# Revit family: MI-FISH
name_source: partatom
category: Plumbing Fixtures
units: mm (PartAtom-declared; Revit-internal decimal feet)

## family parameters
Classification Number = 23.45.30.00
Cut with Voids When Loaded = No
Enable Cutting in Views = No
Host = Face
Maintain Annotation Orientation = No
Part Type = Normal
Room Calculation Point = No
Round Connector Dimension = Use Radius
Shared = No

## types (12) — shared parameters
Assembly Code = D2090300
Description = Fish Scale Interceptor
Interceptor Material = Acid Resistant Epoxy Coated Green
Manufacturer = MIFAB
URL = www.mifab.com
zero-valued in all types: Default Elevation, WFU

## per-type parameters (varying)
| type | A | B | C | D | E | F | Standard Inlet And Outlet Radii | Water Capacity |
| MI-FISH-1 | 29.5 " | 20 " | 3 " | 17 " | 20 " | 2 " | 1 " | 34.29 Gallons |
| MI-FISH-2 | 29.5 " | 20.5 " | 4 " | 20 " | 24 " | 3 " | 1.5 " | 40.74 Gallons |
| MI-FISH-3 | 33.5 " | 26 " | 4 " | 26 " | 30 " | 3 " | 1.5 " | 80.18 Gallons |
| MI-FISH-4 | 37.5 " | 30 " | 4 " | 28 " | 32 " | 3 " | 1.5 " | 114.03 Gallons |
| MI-FISH-5 | 55.5 " | 26 " | 6 " | 30 " | 36 " | 4 " | 2 " | 155.64 Gallons |
| MI-FISH-6 | 67.5 " | 28 " | 8 " | 32 " | 40 " | 6 " | 3 " | 213.80 Gallons |
| MI-FISH-7 | 67.5 " | 28 " | 10 " | 44 " | 54 " | 6 " | 3 " | 302.26 Gallons |
| MI-FISH-8 | 67.5 " | 30 " | 12 " | 54 " | 66 " | 6 " | 3 " | 404.91 Gallons |
| MI-FISH-9 | 67.5 " | 40 " | 10 " | 50 " | 60 " | 6 " | 3 " | 506.42 Gallons |
| MI-FISH-10 | 91.5 " | 40 " | 8 " | 54 " | 62 " | 6 " | 3 " | 868.65 Gallons |
| MI-FISH-11 | 98 " | 50 " | 12 " | 54 " | 66 " | 6 " | 3 " | 1017.35 Gallons |
| MI-FISH-12 | 98 " | 50 " | 12 " | 80 " | 92 " | 6 " | 3 " | 1536 Gallons |

note: column(s) folded — value = type name in every type: Model

## geometry (parser evidence)
native form markers: Blend x3, Sweep x2
no freeform markers — native parametric forms only
